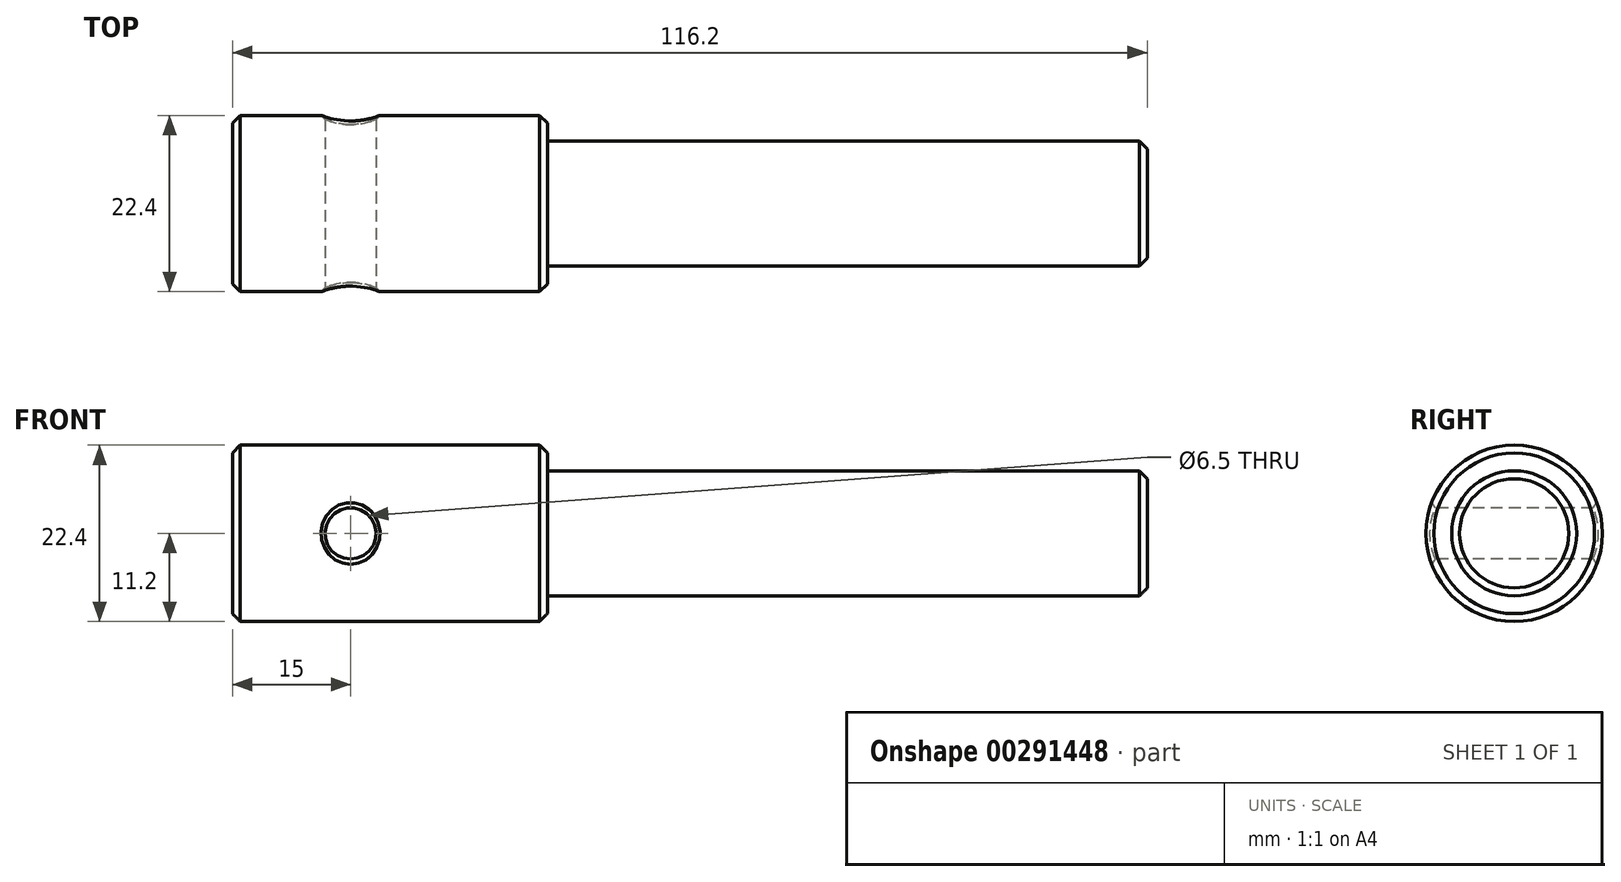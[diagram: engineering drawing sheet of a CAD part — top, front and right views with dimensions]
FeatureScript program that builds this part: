
annotation { "Feature Type Name" : "Feature", "Feature Type Description" : "" }
export const myFeature = defineFeature(function(context is Context, id is Id, definition is map)
    precondition{}
    {
        {
            var Q0;
            Q0=qCreatedBy(makeId("Right.planeOp"),FACE);
            var sketch = newSketch(context, id + "F0", { "sketchPlane" : qUnion([Q0])});
            skCircle(sketch, "E0", {"center": v(0, 0) * mm, "radius": 11.2 * mm});
            skSolve(sketch);
        }
        {
            var Q0;
            Q0=makeQuery(id+"F0.imprint","IMPRINT",FACE,{"disambiguationData":[TD([[makeQuery(id+"F0.imprint","IMPRINT",EDGE,{"derivedFrom":sQuery(id+"F0.wireOp",EDGE,"E0")}),1.0]])]});
            extrude(context, id + "F1", {"entities" : qUnion([Q0]), "depth" : 40 * mm});
        }
        {
            var Q0;
            Q0=qCreatedBy(makeId("Front.planeOp"),FACE);
            var sketch = newSketch(context, id + "F2", { "sketchPlane" : qUnion([Q0])});
            skCircle(sketch, "E1", {"center": v(15, 0) * mm, "radius": 3.25 * mm});
            skSolve(sketch);
        }
        {
            var Q0;
            Q0=makeQuery(id+"F1.opExtrude","CAP_FACE",FACE,{"disambiguationData":[OSD([sQuery(id+"F0.wireOp",EDGE,"E0")])],"isStart":false});
            var sketch = newSketch(context, id + "F3", { "sketchPlane" : qUnion([Q0])});
            skCircle(sketch, "E2", {"center": v(0, 0) * mm, "radius": 7.94 * mm});
            skSolve(sketch);
        }
        {
            var Q0;
            Q0=makeQuery(id+"F3.imprint","IMPRINT",FACE,{"disambiguationData":[TD([[makeQuery(id+"F3.imprint","IMPRINT",EDGE,{"derivedFrom":sQuery(id+"F3.wireOp",EDGE,"E2")}),1.0]])]});
            extrude(context, id + "F4", {"entities" : qUnion([Q0]), "operationType" : NewBodyOperationType.ADD, "depth" : (3 * 25.4) * mm});
        }
        {
            var Q0;
            Q0 = qSketchRegion(id + "F2", true);
            extrude(context, id + "F5", {"entities" : qUnion([Q0]), "operationType" : NewBodyOperationType.REMOVE, "oppositeDirection" : true, "depth" : 25 * mm, "hasSecondDirection" : true, "secondDirectionOppositeDirection" : false, "secondDirectionDepth" : 25 * mm});
        }
        {
            var Q0;
            Q0=makeQuery(id+"F1.opExtrude","CAP_EDGE",EDGE,{"disambiguationData":[OSD([sQuery(id+"F0.wireOp",EDGE,"E0")])],"isStart":true});
            var Q1;
            Q1=makeQuery(id+"F1.opExtrude","CAP_EDGE",EDGE,{"disambiguationData":[OSD([sQuery(id+"F0.wireOp",EDGE,"E0")])],"isStart":false});
            var Q2;
            Q2=makeQuery(id+"F4.opExtrude","CAP_EDGE",EDGE,{"disambiguationData":[OSD([sQuery(id+"F3.wireOp",EDGE,"E2")])],"isStart":false});
            chamfer(context, id + "F6", {"entities" : qUnion([Q0, Q1, Q2]), "width" : 1 * mm, "tangentPropagation" : true});
        }
        {
            var Q0;
            Q0=makeQuery(id+"F5.boolean.opBoolean","INTERSECT",EDGE,{"disambiguationData":[OD(0.0)],"derivedFrom":[makeQuery(id+"F1.opExtrude","SWEPT_FACE",FACE,{"disambiguationData":[OSD([sQuery(id+"F0.wireOp",EDGE,"E0")])]}),makeQuery(id+"F5.opExtrude","SWEPT_FACE",FACE,{"disambiguationData":[OSD([sQuery(id+"F2.wireOp",EDGE,"E1")])]})]});
            var Q1;
            Q1=makeQuery(id+"F5.boolean.opBoolean","INTERSECT",EDGE,{"disambiguationData":[OD(1.0)],"derivedFrom":[makeQuery(id+"F1.opExtrude","SWEPT_FACE",FACE,{"disambiguationData":[OSD([sQuery(id+"F0.wireOp",EDGE,"E0")])]}),makeQuery(id+"F5.opExtrude","SWEPT_FACE",FACE,{"disambiguationData":[OSD([sQuery(id+"F2.wireOp",EDGE,"E1")])]})]});
            chamfer(context, id + "F7", {"entities" : qUnion([Q0, Q1]), "width" : .5 * mm, "tangentPropagation" : true});
        }
    });
